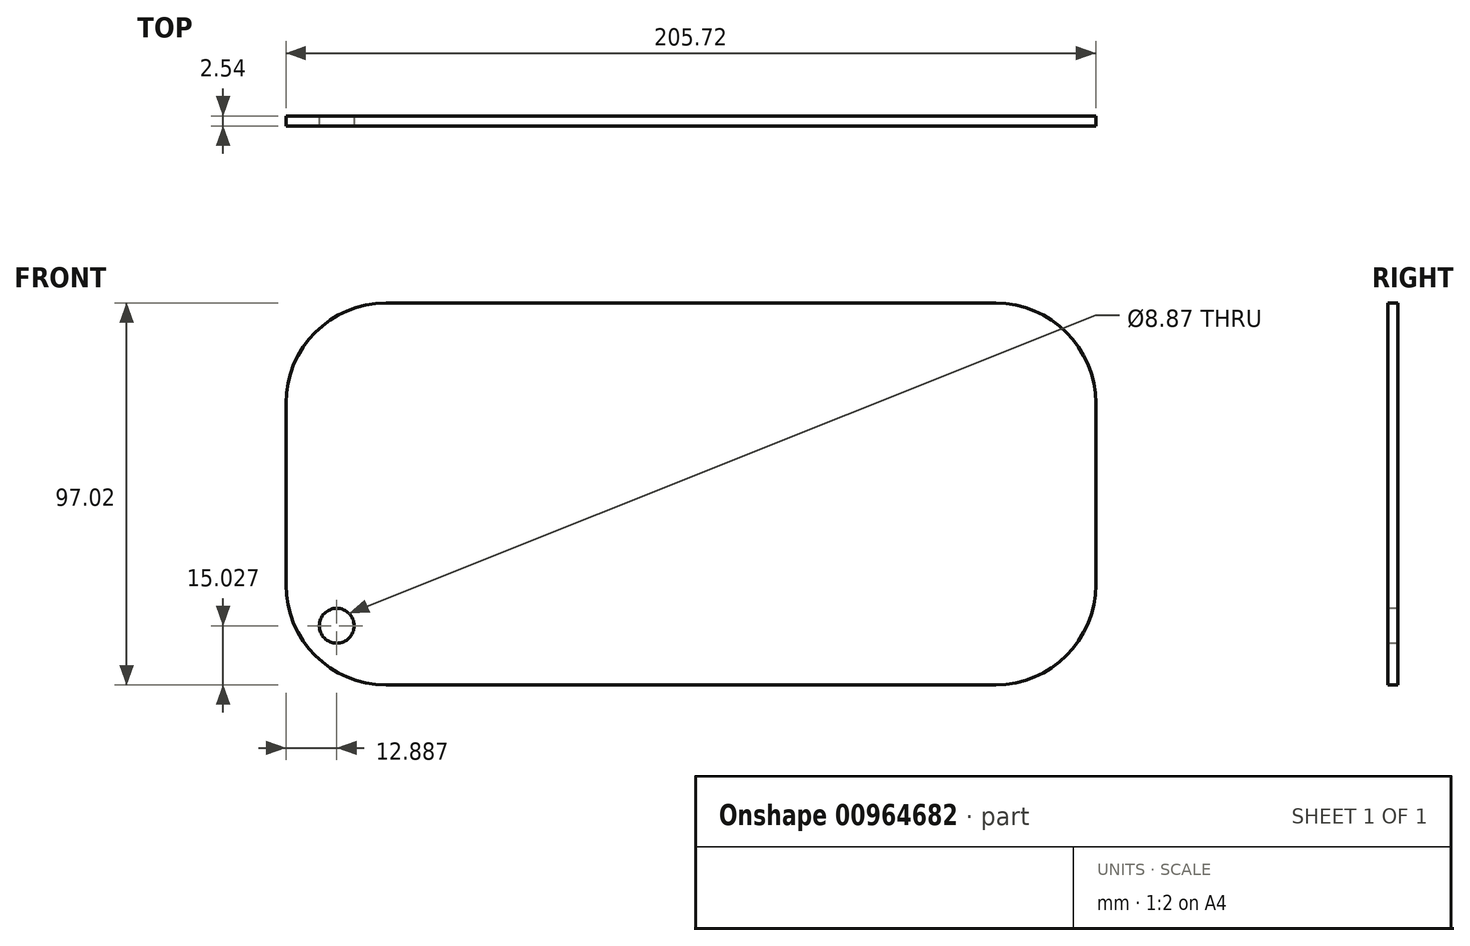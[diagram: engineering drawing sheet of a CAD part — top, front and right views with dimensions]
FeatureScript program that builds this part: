
annotation { "Feature Type Name" : "Feature", "Feature Type Description" : "" }
export const myFeature = defineFeature(function(context is Context, id is Id, definition is map)
    precondition{}
    {
        {
            var Q0;
            Q0=qCreatedBy(makeId("Front.planeOp"),FACE);
            var sketch = newSketch(context, id + "F0", { "sketchPlane" : qUnion([Q0])});
            skLineSegment(sketch, "E0.bottom", {"start": v(102.86, 48.5) * mm, "end": v(-102.86, 48.5) * mm});
            skLineSegment(sketch, "E0.top", {"start": v(102.86, -48.5) * mm, "end": v(-102.86, -48.5) * mm});
            skLineSegment(sketch, "E0.left", {"start": v(102.86, 48.5) * mm, "end": v(102.86, -48.5) * mm});
            skLineSegment(sketch, "E0.right", {"start": v(-102.86, 48.5) * mm, "end": v(-102.86, -48.5) * mm});
            skPoint(sketch, "E0.middle", {"position": v(0, 0) * mm});
            skSolve(sketch);
        }
        {
            var Q0;
            Q0 = qSketchRegion(id + "F0", true);
            extrude(context, id + "F1", {"entities" : qUnion([Q0]), "depth" : 2.54 * mm, "offsetDistance" : 25.4 * mm});
        }
        {
            var Q0;
            Q0=makeQuery(id+"F1.opExtrude","SWEPT_EDGE",EDGE,{"disambiguationData":[OSD([sQuery(id+"F0.wireOp",EDGE,"E0.bottom"),sQuery(id+"F0.wireOp",EDGE,"E0.left")])]});
            var Q1;
            Q1=makeQuery(id+"F1.opExtrude","SWEPT_EDGE",EDGE,{"disambiguationData":[OSD([sQuery(id+"F0.wireOp",EDGE,"E0.top"),sQuery(id+"F0.wireOp",EDGE,"E0.left")])]});
            var Q2;
            Q2=makeQuery(id+"F1.opExtrude","SWEPT_EDGE",EDGE,{"disambiguationData":[OSD([sQuery(id+"F0.wireOp",EDGE,"E0.top"),sQuery(id+"F0.wireOp",EDGE,"E0.right")])]});
            var Q3;
            Q3=makeQuery(id+"F1.opExtrude","SWEPT_EDGE",EDGE,{"disambiguationData":[OSD([sQuery(id+"F0.wireOp",EDGE,"E0.bottom"),sQuery(id+"F0.wireOp",EDGE,"E0.right")])]});
            fillet(context, id + "F2", {"entities" : qUnion([Q0, Q1, Q2, Q3]), "radius" : 25.4 * mm, "tangentPropagation" : true, "allowEdgeOverflow" : false});
        }
        {
            var Q0;
            Q0=makeQuery(id+"F1.opExtrude","CAP_FACE",FACE,{"disambiguationData":[OSD([sQuery(id+"F0.wireOp",EDGE,"E0.bottom"),sQuery(id+"F0.wireOp",EDGE,"E0.top"),sQuery(id+"F0.wireOp",EDGE,"E0.left"),sQuery(id+"F0.wireOp",EDGE,"E0.right")])],"isStart":false});
            var sketch = newSketch(context, id + "F3", { "sketchPlane" : qUnion([Q0])});
            skCircle(sketch, "E1", {"center": v(-89.97, -33.48) * mm, "radius": 4.44 * mm});
            skSolve(sketch);
        }
        {
            var Q0;
            Q0 = qSketchRegion(id + "F3", true);
            extrude(context, id + "F4", {"entities" : qUnion([Q0]), "operationType" : NewBodyOperationType.REMOVE, "oppositeDirection" : true, "depth" : 2.54 * mm, "offsetDistance" : 25.4 * mm});
        }
    });
